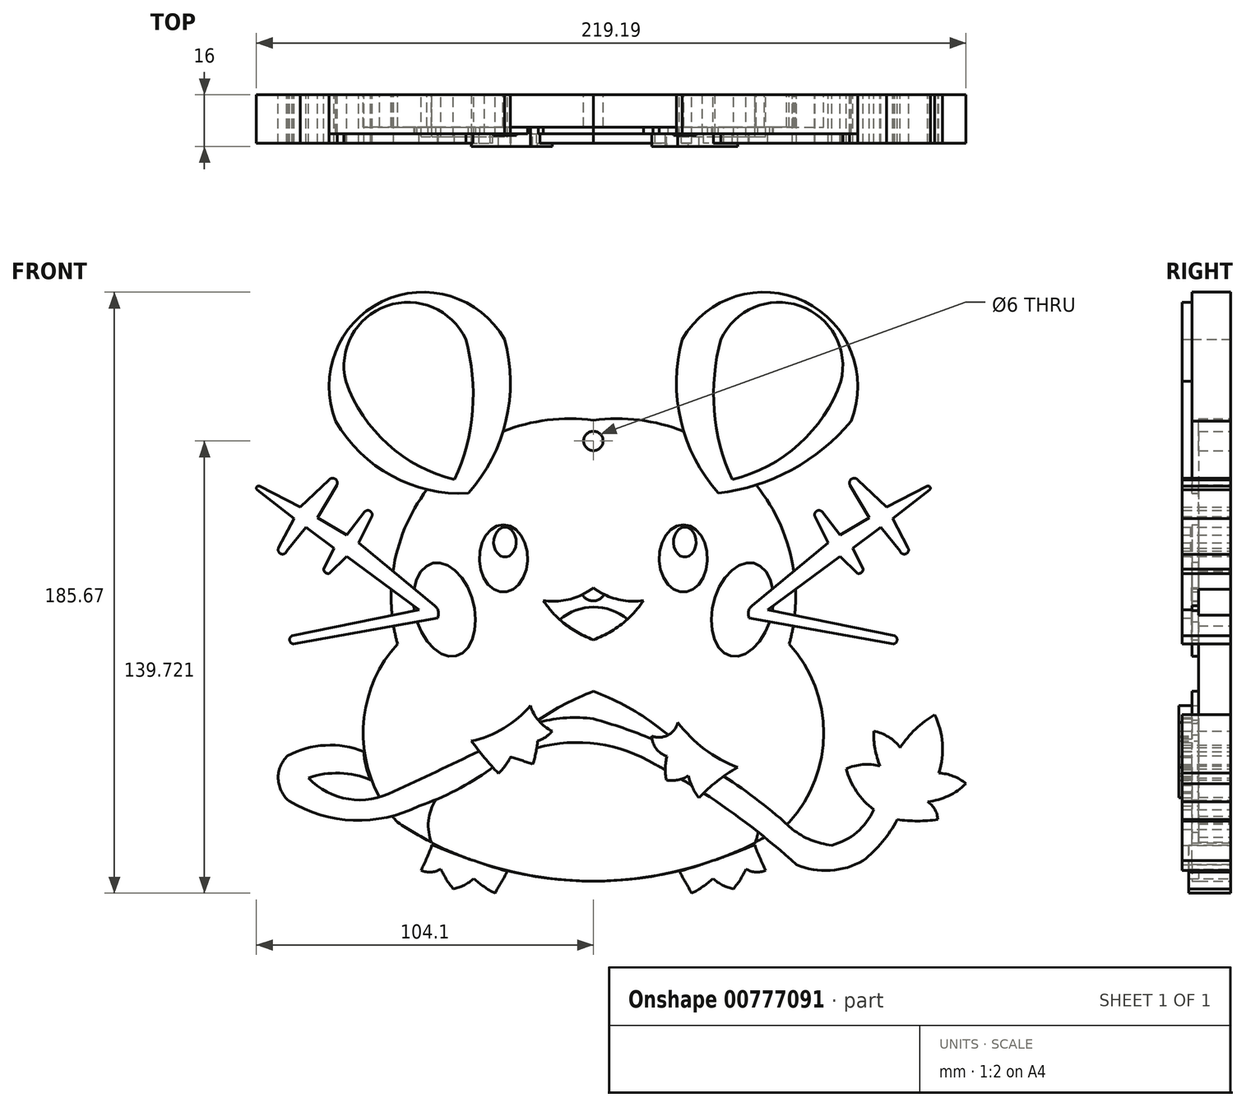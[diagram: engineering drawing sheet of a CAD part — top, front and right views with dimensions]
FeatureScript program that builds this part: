
annotation { "Feature Type Name" : "Feature", "Feature Type Description" : "" }
export const myFeature = defineFeature(function(context is Context, id is Id, definition is map)
    precondition{}
    {
        {
            var Q0;
            Q0=qCreatedBy(makeId("Front.planeOp"),FACE);
            var sketch = newSketch(context, id + "F0", { "sketchPlane" : qUnion([Q0])});
            skPoint(sketch, "E0", {"position": v(-60.51, 0) * mm});
            skPoint(sketch, "E1", {"position": v(0, 69.06) * mm});
            skArc(sketch, "E2", {"start": v(0, 69.06) * mm, "mid": v(-48.84, 50.82) * mm, "end": v(-60.51, 0) * mm});
            skLineSegment(sketch, "E3", {"start": v(0, 69.06) * mm, "end": v(0, -72.21) * mm, "construction": true});
            skArc(sketch, "E4.MirrorCS", {"start": v(0, 69.06) * mm, "mid": v(48.84, 50.82) * mm, "end": v(60.51, 0) * mm});
            skPoint(sketch, "E5", {"position": v(-60.51, -55.13) * mm});
            skArc(sketch, "E6", {"start": v(-60.51, 0) * mm, "mid": v(-71.12, -27.56) * mm, "end": v(-60.51, -55.13) * mm});
            skArc(sketch, "E7.MirrorCS", {"start": v(60.51, 0) * mm, "mid": v(71.12, -27.56) * mm, "end": v(60.51, -55.13) * mm});
            skArc(sketch, "E8", {"start": v(-60.51, -55.13) * mm, "mid": v(0, -73.32) * mm, "end": v(60.51, -55.13) * mm});
            skSolve(sketch);
        }
        {
            var Q0;
            Q0=qCreatedBy(makeId("Front.planeOp"),FACE);
            var sketch = newSketch(context, id + "F1", { "sketchPlane" : qUnion([Q0])});
            skEllipse(sketch, "E9", {"center": v(-27.78, 26.42) * mm, "majorRadius": 10.45 * mm, "minorRadius": 7.45 * mm, "majorAxis": v(0, 1)});
            skEllipse(sketch, "E10", {"center": v(-46, 10.64) * mm, "majorRadius": 14.77 * mm, "minorRadius": 9.16 * mm, "majorAxis": v(-0.25, 0.97)});
            skEllipse(sketch, "E11.MirrorC", {"center": v(46, 10.64) * mm, "majorRadius": 14.77 * mm, "minorRadius": 9.16 * mm, "majorAxis": v(0.25, 0.97)});
            skEllipse(sketch, "E12.MirrorC", {"center": v(27.78, 26.42) * mm, "majorRadius": 10.45 * mm, "minorRadius": 7.45 * mm, "majorAxis": v(0, 1)});
            skEllipse(sketch, "E13", {"center": v(-27.3, 31.45) * mm, "majorRadius": 4.6 * mm, "minorRadius": 3.5 * mm, "majorAxis": v(0, 1)});
            skPoint(sketch, "E14.endSnap0", {"position": v(-30.8, 31.45) * mm});
            skPoint(sketch, "E15", {"position": v(-34.3, 31.45) * mm});
            skPoint(sketch, "E16", {"position": v(21.25, 31.45) * mm});
            skPoint(sketch, "E17", {"position": v(28.25, 31.45) * mm});
            skPoint(sketch, "E18", {"position": v(-27.3, 36.05) * mm});
            skLineSegment(sketch, "E19", {"start": v(28.25, 36.05) * mm, "end": v(28.25, 40.65) * mm});
            skPoint(sketch, "E20", {"position": v(28.25, 36.05) * mm});
            skEllipse(sketch, "E21", {"center": v(28.25, 31.45) * mm, "majorRadius": 4.6 * mm, "minorRadius": 3.5 * mm, "majorAxis": v(0, 1)});
            skPoint(sketch, "E22", {"position": v(-23.8, 31.45) * mm});
            skPoint(sketch, "E23", {"position": v(24.75, 31.45) * mm});
            skPoint(sketch, "E24", {"position": v(31.75, 31.45) * mm});
            skPoint(sketch, "E14.end.orphan", {"position": v(-36.36, 31.45) * mm});
            skPoint(sketch, "E25", {"position": v(0, 17.34) * mm});
            skPoint(sketch, "E26", {"position": v(-18.45, 14.06) * mm});
            skArc(sketch, "E27", {"start": v(-18.45, 14.06) * mm, "mid": v(-8.83, 13.48) * mm, "end": v(0, 17.34) * mm});
            skArc(sketch, "E28.MirrorCS", {"start": v(18.45, 14.06) * mm, "mid": v(8.83, 13.48) * mm, "end": v(0, 17.34) * mm});
            skPoint(sketch, "E29", {"position": v(0, 0) * mm});
            skPoint(sketch, "E30", {"position": v(0, 1.29) * mm});
            skPoint(sketch, "E31", {"position": v(0, 10.13) * mm});
            skPoint(sketch, "E32", {"position": v(-5.69, 14.3) * mm});
            skArc(sketch, "E33", {"start": v(-5.69, 14.3) * mm, "mid": v(-3.15, 11.8) * mm, "end": v(0, 10.13) * mm});
            skArc(sketch, "E34.MirrorCS", {"start": v(5.69, 14.3) * mm, "mid": v(3.15, 11.8) * mm, "end": v(0, 10.13) * mm});
            skArc(sketch, "E35", {"start": v(-15.44, 13.38) * mm, "mid": v(-8.7, 6.08) * mm, "end": v(0, 1.29) * mm});
            skArc(sketch, "E36.MirrorCS", {"start": v(15.44, 13.38) * mm, "mid": v(8.7, 6.08) * mm, "end": v(0, 1.29) * mm});
            skPoint(sketch, "E37", {"position": v(-79.58, 68.87) * mm});
            skPoint(sketch, "E38", {"position": v(-38.6, 46.57) * mm});
            skPoint(sketch, "E39", {"position": v(-27.45, 94.11) * mm});
            skArc(sketch, "E40", {"start": v(-79.58, 68.87) * mm, "mid": v(-62.27, 51.88) * mm, "end": v(-38.6, 46.57) * mm});
            skArc(sketch, "E41", {"start": v(-38.6, 46.57) * mm, "mid": v(-27, 68.93) * mm, "end": v(-27.45, 94.11) * mm});
            skArc(sketch, "E42", {"start": v(-27.45, 94.11) * mm, "mid": v(-65.26, 105.75) * mm, "end": v(-79.58, 68.87) * mm});
            skArc(sketch, "E43.MirrorCS", {"start": v(38.6, 46.57) * mm, "mid": v(27, 68.93) * mm, "end": v(27.45, 94.11) * mm});
            skArc(sketch, "E44.MirrorCS", {"start": v(27.45, 94.11) * mm, "mid": v(65.26, 105.75) * mm, "end": v(79.58, 68.87) * mm});
            skArc(sketch, "E45", {"start": v(38.6, 46.57) * mm, "mid": v(61.26, 53.74) * mm, "end": v(79.58, 68.87) * mm});
            skPoint(sketch, "E46", {"position": v(0, -14.65) * mm});
            skPoint(sketch, "E47", {"position": v(-18.44, -24.49) * mm});
            skPoint(sketch, "E48", {"position": v(-49.92, -61.53) * mm});
            skPoint(sketch, "E49", {"position": v(-48.16, -47.4) * mm});
            skArc(sketch, "E50", {"start": v(0, -14.65) * mm, "mid": v(-9.54, -18.97) * mm, "end": v(-18.44, -24.49) * mm});
            skArc(sketch, "E51", {"start": v(-48.16, -47.4) * mm, "mid": v(-50.9, -54.23) * mm, "end": v(-49.92, -61.53) * mm});
            skLineSegment(sketch, "E52", {"start": v(-18.44, -24.49) * mm, "end": v(-48.16, -47.4) * mm});
            skArc(sketch, "E53.MirrorCS", {"start": v(0, -14.65) * mm, "mid": v(9.54, -18.97) * mm, "end": v(18.44, -24.49) * mm});
            skLineSegment(sketch, "E54.MirrorCS", {"start": v(18.44, -24.49) * mm, "end": v(48.16, -47.4) * mm});
            skArc(sketch, "E55.MirrorCS", {"start": v(48.16, -47.4) * mm, "mid": v(50.9, -54.23) * mm, "end": v(49.92, -61.53) * mm});
            skArc(sketch, "E56", {"start": v(-49.92, -61.53) * mm, "mid": v(0, -73.23) * mm, "end": v(49.92, -61.53) * mm});
            skSolve(sketch);
        }
        {
            var Q0;
            Q0=qCreatedBy(makeId("Front.planeOp"),FACE);
            var sketch = newSketch(context, id + "F2", { "sketchPlane" : qUnion([Q0])});
            skLineSegment(sketch, "E57", {"start": v(-48.16, 7.98) * mm, "end": v(-92.67, 0) * mm});
            skPoint(sketch, "E58", {"position": v(-93.06, 2.5) * mm});
            skPoint(sketch, "E59", {"position": v(-48.96, 11.76) * mm});
            skArc(sketch, "E60", {"start": v(-93.06, 2.5) * mm, "mid": v(-93.82, 1.1) * mm, "end": v(-92.67, 0) * mm});
            skArc(sketch, "E61", {"start": v(-48.16, 7.98) * mm, "mid": v(-47.9, 10.01) * mm, "end": v(-48.96, 11.76) * mm});
            skLineSegment(sketch, "E62", {"start": v(-93.06, 2.5) * mm, "end": v(-53.87, 10.6) * mm});
            skLineSegment(sketch, "E63", {"start": v(-53.87, 10.6) * mm, "end": v(-76.2, 27) * mm});
            skLineSegment(sketch, "E64", {"start": v(-76.2, 27) * mm, "end": v(-81.72, 21.76) * mm});
            skLineSegment(sketch, "E65", {"start": v(-48.96, 11.76) * mm, "end": v(-72.48, 31.21) * mm});
            skLineSegment(sketch, "E66", {"start": v(-72.48, 31.21) * mm, "end": v(-68.43, 39.4) * mm});
            skPoint(sketch, "E67", {"position": v(-83.3, 23.07) * mm});
            skPoint(sketch, "E68", {"position": v(-70.75, 40.72) * mm});
            skPoint(sketch, "E69", {"position": v(-79.3, 48.99) * mm});
            skPoint(sketch, "E70", {"position": v(-81.72, 50.64) * mm});
            skPoint(sketch, "E71", {"position": v(-103.83, 47.6) * mm});
            skPoint(sketch, "E72", {"position": v(-103.15, 48.71) * mm});
            skPoint(sketch, "E73", {"position": v(-97.22, 29.69) * mm});
            skPoint(sketch, "E74", {"position": v(-94.74, 28.72) * mm});
            skLineSegment(sketch, "E75", {"start": v(-80.13, 29.55) * mm, "end": v(-87.57, 35.2) * mm});
            skLineSegment(sketch, "E76", {"start": v(-79.3, 48.99) * mm, "end": v(-85.23, 38.92) * mm});
            skLineSegment(sketch, "E77", {"start": v(-85.23, 38.92) * mm, "end": v(-76.2, 33.6) * mm});
            skLineSegment(sketch, "E78", {"start": v(-76.2, 33.6) * mm, "end": v(-70.75, 40.72) * mm});
            skLineSegment(sketch, "E79", {"start": v(-97.22, 29.69) * mm, "end": v(-92.4, 38.79) * mm});
            skLineSegment(sketch, "E80", {"start": v(-92.4, 38.79) * mm, "end": v(-103.83, 47.6) * mm});
            skLineSegment(sketch, "E81", {"start": v(-103.15, 48.71) * mm, "end": v(-90.6, 42.23) * mm});
            skLineSegment(sketch, "E82", {"start": v(-90.6, 42.23) * mm, "end": v(-81.72, 50.64) * mm});
            skArc(sketch, "E83", {"start": v(-103.15, 48.71) * mm, "mid": v(-104, 48.48) * mm, "end": v(-103.83, 47.6) * mm});
            skArc(sketch, "E84", {"start": v(-97.22, 29.69) * mm, "mid": v(-96.52, 27.81) * mm, "end": v(-94.74, 28.72) * mm});
            skLineSegment(sketch, "E85", {"start": v(-94.74, 28.72) * mm, "end": v(-88.74, 36.09) * mm});
            skLineSegment(sketch, "E86", {"start": v(-88.74, 36.09) * mm, "end": v(-87.57, 35.2) * mm});
            skArc(sketch, "E87", {"start": v(-79.3, 48.99) * mm, "mid": v(-79.73, 50.94) * mm, "end": v(-81.72, 50.64) * mm});
            skArc(sketch, "E88", {"start": v(-68.43, 39.4) * mm, "mid": v(-69.02, 41.07) * mm, "end": v(-70.75, 40.72) * mm});
            skArc(sketch, "E89", {"start": v(-83.3, 23.07) * mm, "mid": v(-82.8, 22.05) * mm, "end": v(-81.72, 21.76) * mm});
            skLineSegment(sketch, "E90", {"start": v(-80.13, 29.55) * mm, "end": v(-83.3, 23.07) * mm});
            skLineSegment(sketch, "E91.MirrorCS", {"start": v(103.15, 48.71) * mm, "end": v(90.6, 42.23) * mm});
            skArc(sketch, "E92.MirrorCS", {"start": v(103.15, 48.71) * mm, "mid": v(104, 48.48) * mm, "end": v(103.83, 47.6) * mm});
            skLineSegment(sketch, "E93.MirrorCS", {"start": v(92.4, 38.79) * mm, "end": v(103.83, 47.6) * mm});
            skLineSegment(sketch, "E94.MirrorCS", {"start": v(90.6, 42.23) * mm, "end": v(81.72, 50.64) * mm});
            skArc(sketch, "E95.MirrorCS", {"start": v(79.3, 48.99) * mm, "mid": v(79.73, 50.94) * mm, "end": v(81.72, 50.64) * mm});
            skLineSegment(sketch, "E96.MirrorCS", {"start": v(79.3, 48.99) * mm, "end": v(85.23, 38.92) * mm});
            skLineSegment(sketch, "E97.MirrorCS", {"start": v(97.22, 29.69) * mm, "end": v(92.4, 38.79) * mm});
            skArc(sketch, "E98.MirrorCS", {"start": v(97.22, 29.69) * mm, "mid": v(96.52, 27.81) * mm, "end": v(94.74, 28.72) * mm});
            skLineSegment(sketch, "E99.MirrorCS", {"start": v(94.74, 28.72) * mm, "end": v(88.74, 36.09) * mm});
            skLineSegment(sketch, "E100.MirrorCS", {"start": v(80.13, 29.55) * mm, "end": v(87.57, 35.2) * mm});
            skLineSegment(sketch, "E101.MirrorCS", {"start": v(88.74, 36.09) * mm, "end": v(87.57, 35.2) * mm});
            skLineSegment(sketch, "E102.MirrorCS", {"start": v(80.13, 29.55) * mm, "end": v(83.3, 23.07) * mm});
            skArc(sketch, "E103.MirrorCS", {"start": v(83.3, 23.07) * mm, "mid": v(82.8, 22.05) * mm, "end": v(81.72, 21.76) * mm});
            skLineSegment(sketch, "E104.MirrorCS", {"start": v(76.2, 27) * mm, "end": v(81.72, 21.76) * mm});
            skLineSegment(sketch, "E105.MirrorCS", {"start": v(53.87, 10.6) * mm, "end": v(76.2, 27) * mm});
            skLineSegment(sketch, "E106.MirrorCS", {"start": v(76.2, 33.6) * mm, "end": v(70.75, 40.72) * mm});
            skArc(sketch, "E107.MirrorCS", {"start": v(68.43, 39.4) * mm, "mid": v(69.02, 41.07) * mm, "end": v(70.75, 40.72) * mm});
            skLineSegment(sketch, "E108.MirrorCS", {"start": v(72.48, 31.21) * mm, "end": v(68.43, 39.4) * mm});
            skLineSegment(sketch, "E109.MirrorCS", {"start": v(48.96, 11.76) * mm, "end": v(72.48, 31.21) * mm});
            skArc(sketch, "E110.MirrorCS", {"start": v(48.16, 7.98) * mm, "mid": v(47.9, 10.01) * mm, "end": v(48.96, 11.76) * mm});
            skLineSegment(sketch, "E111.MirrorCS", {"start": v(48.16, 7.98) * mm, "end": v(92.67, 0) * mm});
            skLineSegment(sketch, "E112.MirrorCS", {"start": v(93.06, 2.5) * mm, "end": v(53.87, 10.6) * mm});
            skArc(sketch, "E113.MirrorCS", {"start": v(93.06, 2.5) * mm, "mid": v(93.82, 1.1) * mm, "end": v(92.67, 0) * mm});
            skPoint(sketch, "E114", {"position": v(-70.89, -33.3) * mm});
            skPoint(sketch, "E115", {"position": v(-94.5, -34.6) * mm});
            skPoint(sketch, "E116", {"position": v(-94, -48.54) * mm});
            skPoint(sketch, "E117", {"position": v(-53.84, -50.01) * mm});
            skPoint(sketch, "E118", {"position": v(-31.87, -38.7) * mm});
            skPoint(sketch, "E119", {"position": v(19.1, -37.23) * mm});
            skPoint(sketch, "E120", {"position": v(62.71, -68.21) * mm});
            skPoint(sketch, "E121", {"position": v(83.37, -66.9) * mm});
            skPoint(sketch, "E122", {"position": v(93.86, -54.29) * mm});
            skPoint(sketch, "E123", {"position": v(106.4, -54.29) * mm});
            skPoint(sketch, "E124", {"position": v(103.29, -48.74) * mm});
            skPoint(sketch, "E125", {"position": v(115.1, -43.17) * mm});
            skPoint(sketch, "E126", {"position": v(106.73, -39.89) * mm});
            skPoint(sketch, "E127", {"position": v(105.42, -21.85) * mm});
            skPoint(sketch, "E128", {"position": v(94.76, -32.02) * mm});
            skPoint(sketch, "E129", {"position": v(86.57, -26.94) * mm});
            skPoint(sketch, "E130", {"position": v(88.54, -37.76) * mm});
            skPoint(sketch, "E131", {"position": v(78.04, -38.58) * mm});
            skPoint(sketch, "E132", {"position": v(86.57, -51.2) * mm});
            skPoint(sketch, "E133", {"position": v(73.62, -62.18) * mm});
            skPoint(sketch, "E134", {"position": v(61.49, -57.26) * mm});
            skPoint(sketch, "E135", {"position": v(0, -23.17) * mm});
            skPoint(sketch, "E136", {"position": v(-18.84, -24.8) * mm});
            skArc(sketch, "E137", {"start": v(94.76, -32.02) * mm, "mid": v(91.14, -28.71) * mm, "end": v(86.57, -26.94) * mm});
            skArc(sketch, "E138", {"start": v(105.42, -21.85) * mm, "mid": v(99.52, -26.34) * mm, "end": v(94.76, -32.02) * mm});
            skArc(sketch, "E139", {"start": v(106.73, -39.89) * mm, "mid": v(107.82, -30.74) * mm, "end": v(105.42, -21.85) * mm});
            skArc(sketch, "E140", {"start": v(115.1, -43.17) * mm, "mid": v(111.17, -40.86) * mm, "end": v(106.73, -39.89) * mm});
            skArc(sketch, "E141", {"start": v(103.29, -48.74) * mm, "mid": v(109.66, -46.95) * mm, "end": v(115.1, -43.17) * mm});
            skArc(sketch, "E142", {"start": v(106.4, -54.29) * mm, "mid": v(105.49, -51.15) * mm, "end": v(103.29, -48.74) * mm});
            skArc(sketch, "E143", {"start": v(93.86, -54.29) * mm, "mid": v(100.13, -54.7) * mm, "end": v(106.4, -54.29) * mm});
            skArc(sketch, "E144", {"start": v(78.04, -38.58) * mm, "mid": v(81.27, -45.59) * mm, "end": v(86.57, -51.2) * mm});
            skArc(sketch, "E145", {"start": v(88.54, -37.76) * mm, "mid": v(83.22, -37.27) * mm, "end": v(78.04, -38.58) * mm});
            skArc(sketch, "E146", {"start": v(86.57, -26.94) * mm, "mid": v(87.01, -32.44) * mm, "end": v(88.54, -37.76) * mm});
            skArc(sketch, "E147", {"start": v(73.62, -62.18) * mm, "mid": v(81.39, -58.21) * mm, "end": v(86.57, -51.2) * mm});
            skArc(sketch, "E148", {"start": v(61.49, -57.26) * mm, "mid": v(67.2, -60.57) * mm, "end": v(73.62, -62.18) * mm});
            skArc(sketch, "E149", {"start": v(61.49, -57.26) * mm, "mid": v(32.8, -36.5) * mm, "end": v(0, -23.17) * mm});
            skArc(sketch, "E150", {"start": v(0, -23.17) * mm, "mid": v(-9.51, -22.93) * mm, "end": v(-18.84, -24.8) * mm});
            skArc(sketch, "E151", {"start": v(83.37, -66.9) * mm, "mid": v(89.26, -61.14) * mm, "end": v(93.86, -54.29) * mm});
            skArc(sketch, "E152", {"start": v(62.71, -68.21) * mm, "mid": v(73.2, -69.99) * mm, "end": v(83.37, -66.9) * mm});
            skArc(sketch, "E153", {"start": v(62.71, -68.21) * mm, "mid": v(41.87, -51.37) * mm, "end": v(19.1, -37.23) * mm});
            skArc(sketch, "E154", {"start": v(19.1, -37.23) * mm, "mid": v(-6.6, -30.48) * mm, "end": v(-31.87, -38.7) * mm});
            skArc(sketch, "E155", {"start": v(-53.84, -50.01) * mm, "mid": v(-42.41, -45.22) * mm, "end": v(-31.87, -38.7) * mm});
            skArc(sketch, "E156", {"start": v(-94, -48.54) * mm, "mid": v(-74.11, -54.48) * mm, "end": v(-53.84, -50.01) * mm});
            skArc(sketch, "E157", {"start": v(-94.5, -34.6) * mm, "mid": v(-97.37, -41.68) * mm, "end": v(-94, -48.54) * mm});
            skArc(sketch, "E158", {"start": v(-70.89, -33.3) * mm, "mid": v(-82.84, -31.32) * mm, "end": v(-94.5, -34.6) * mm});
            skArc(sketch, "E159", {"start": v(-70.89, -33.3) * mm, "mid": v(-70.25, -37.76) * mm, "end": v(-68.8, -42.03) * mm});
            skArc(sketch, "E160", {"start": v(-68.8, -42.03) * mm, "mid": v(-78.34, -39.94) * mm, "end": v(-88.02, -41.35) * mm});
            skArc(sketch, "E161", {"start": v(-88.02, -41.35) * mm, "mid": v(-75.61, -47.94) * mm, "end": v(-61.77, -45.54) * mm});
            skArc(sketch, "E162", {"start": v(-61.77, -45.54) * mm, "mid": v(-40.15, -35.48) * mm, "end": v(-18.84, -24.8) * mm});
            skPoint(sketch, "E163", {"position": v(-49.8, -62.04) * mm});
            skPoint(sketch, "E164", {"position": v(-52.75, -69.75) * mm});
            skPoint(sketch, "E165", {"position": v(-47.17, -69.9) * mm});
            skPoint(sketch, "E166", {"position": v(-43.4, -75.48) * mm});
            skPoint(sketch, "E167", {"position": v(-36.52, -72.53) * mm});
            skPoint(sketch, "E168", {"position": v(-30.45, -77.29) * mm});
            skPoint(sketch, "E169", {"position": v(-26.85, -70.24) * mm});
            skArc(sketch, "E170", {"start": v(-49.8, -62.04) * mm, "mid": v(-51.37, -65.86) * mm, "end": v(-52.75, -69.75) * mm});
            skArc(sketch, "E171", {"start": v(-52.75, -69.75) * mm, "mid": v(-49.97, -70.3) * mm, "end": v(-47.17, -69.9) * mm});
            skArc(sketch, "E172", {"start": v(-47.17, -69.9) * mm, "mid": v(-45.46, -72.81) * mm, "end": v(-43.4, -75.48) * mm});
            skArc(sketch, "E173", {"start": v(-43.4, -75.48) * mm, "mid": v(-39.78, -74.42) * mm, "end": v(-36.52, -72.53) * mm});
            skArc(sketch, "E174", {"start": v(-36.52, -72.53) * mm, "mid": v(-33.57, -75.02) * mm, "end": v(-30.45, -77.29) * mm});
            skArc(sketch, "E175", {"start": v(-30.45, -77.29) * mm, "mid": v(-28.52, -73.83) * mm, "end": v(-26.85, -70.24) * mm});
            skArc(sketch, "E176.MirrorCS", {"start": v(49.8, -62.04) * mm, "mid": v(51.37, -65.86) * mm, "end": v(52.75, -69.75) * mm});
            skArc(sketch, "E177.MirrorCS", {"start": v(52.75, -69.75) * mm, "mid": v(49.97, -70.3) * mm, "end": v(47.17, -69.9) * mm});
            skArc(sketch, "E178.MirrorCS", {"start": v(47.17, -69.9) * mm, "mid": v(45.46, -72.81) * mm, "end": v(43.4, -75.48) * mm});
            skArc(sketch, "E179.MirrorCS", {"start": v(43.4, -75.48) * mm, "mid": v(39.78, -74.42) * mm, "end": v(36.52, -72.53) * mm});
            skArc(sketch, "E180.MirrorCS", {"start": v(36.52, -72.53) * mm, "mid": v(33.57, -75.02) * mm, "end": v(30.45, -77.29) * mm});
            skArc(sketch, "E181.MirrorCS", {"start": v(30.45, -77.29) * mm, "mid": v(28.52, -73.83) * mm, "end": v(26.85, -70.24) * mm});
            skPoint(sketch, "E182", {"position": v(-42.87, 50.73) * mm});
            skPoint(sketch, "E183", {"position": v(-39.4, 94.09) * mm});
            skPoint(sketch, "E184", {"position": v(-76.49, 81.1) * mm});
            skArc(sketch, "E185", {"start": v(-42.87, 50.73) * mm, "mid": v(-37.35, 72.1) * mm, "end": v(-39.4, 94.09) * mm});
            skArc(sketch, "E186", {"start": v(-76.49, 81.1) * mm, "mid": v(-63.51, 61.68) * mm, "end": v(-42.87, 50.73) * mm});
            skArc(sketch, "E187", {"start": v(-39.4, 94.09) * mm, "mid": v(-63.83, 104.42) * mm, "end": v(-76.49, 81.1) * mm});
            skArc(sketch, "E188.MirrorCS", {"start": v(76.49, 81.1) * mm, "mid": v(63.51, 61.68) * mm, "end": v(42.87, 50.73) * mm});
            skArc(sketch, "E189.MirrorCS", {"start": v(39.4, 94.09) * mm, "mid": v(63.83, 104.42) * mm, "end": v(76.49, 81.1) * mm});
            skArc(sketch, "E190.MirrorCS", {"start": v(42.87, 50.73) * mm, "mid": v(37.35, 72.1) * mm, "end": v(39.4, 94.09) * mm});
            skArc(sketch, "E191", {"start": v(-49.73, -62) * mm, "mid": v(-38.7, -67.26) * mm, "end": v(-26.85, -70.24) * mm});
            skArc(sketch, "E192.MirrorCS", {"start": v(49.73, -62) * mm, "mid": v(38.7, -67.26) * mm, "end": v(26.85, -70.24) * mm});
            skLineSegment(sketch, "E193", {"start": v(76.2, 33.6) * mm, "end": v(85.23, 38.92) * mm});
            skSolve(sketch);
        }
        {
            var Q0;
            Q0=qCreatedBy(makeId("Front.planeOp"),FACE);
            var sketch = newSketch(context, id + "F3", { "sketchPlane" : qUnion([Q0])});
            skCircle(sketch, "E194", {"center": v(0, 62.7) * mm, "radius": 4 * mm});
            skSolve(sketch);
        }
        {
            var Q0;
            Q0=qSketchRegion(id+"F0",true);
            extrude(context, id + "F4", {"entities" : qUnion([Q0]), "depth" : 10 * mm, "offsetDistance" : 25 * mm});
        }
        {
            var Q0;
            Q0=qSketchRegion(id+"F1",true);
            extrude(context, id + "F5", {"entities" : qUnion([Q0]), "operationType" : NewBodyOperationType.ADD, "depth" : 12 * mm, "offsetDistance" : 25 * mm});
        }
        {
            var Q0;
            Q0=makeQuery(id+"F5.opExtrude","CAP_FACE",FACE,{"disambiguationData":[OSD([sQuery(id+"F1.wireOp",EDGE,"E27"),sQuery(id+"F1.wireOp",EDGE,"E28.MirrorCS"),sQuery(id+"F1.wireOp",EDGE,"E35"),sQuery(id+"F1.wireOp",EDGE,"E36.MirrorCS")])],"isStart":false});
            var sketch = newSketch(context, id + "F6", { "sketchPlane" : qUnion([Q0])});
            skArc(sketch, "E195", {"start": v(10.55, 7.64) * mm, "mid": v(0.05, 11.38) * mm, "end": v(-10.39, 7.49) * mm});
            skArc(sketch, "E196", {"start": v(-10.39, 7.49) * mm, "mid": v(-5.46, 3.94) * mm, "end": v(0, 1.29) * mm});
            skArc(sketch, "E197", {"start": v(0, 1.29) * mm, "mid": v(5.59, 3.94) * mm, "end": v(10.55, 7.64) * mm});
            skSolve(sketch);
        }
        {
            var Q0;
            Q0=makeQuery(id+"F6.imprint","IMPRINT",FACE,{"disambiguationData":[TD([[makeQuery(id+"F6.imprint","IMPRINT",EDGE,{"derivedFrom":sQuery(id+"F6.wireOp",EDGE,"E195")}),1.0]])]});
            extrude(context, id + "F7", {"entities" : qUnion([Q0]), "operationType" : NewBodyOperationType.ADD, "depth" : 0.1 * mm, "offsetDistance" : 25 * mm});
        }
        {
            var Q0;
            Q0=makeQuery(id+"F5.boolean.opBoolean","SPLIT",FACE,{"disambiguationData":[TD([makeQuery(id+"F5.opExtrude","SWEPT_FACE",FACE,{"disambiguationData":[OSD([sQuery(id+"F1.wireOp",EDGE,"E13")])]})])],"derivedFrom":makeQuery(id+"F4.opExtrude","CAP_FACE",FACE,{"disambiguationData":[OSD([sQuery(id+"F0.wireOp",EDGE,"E2"),sQuery(id+"F0.wireOp",EDGE,"E4.MirrorCS"),sQuery(id+"F0.wireOp",EDGE,"E6"),sQuery(id+"F0.wireOp",EDGE,"E7.MirrorCS"),sQuery(id+"F0.wireOp",EDGE,"E8")])],"isStart":false})});
            var Q1;
            Q1=makeQuery(id+"F5.boolean.opBoolean","SPLIT",FACE,{"disambiguationData":[TD([makeQuery(id+"F5.opExtrude","SWEPT_FACE",FACE,{"disambiguationData":[OSD([sQuery(id+"F1.wireOp",EDGE,"E21")])]})])],"derivedFrom":makeQuery(id+"F4.opExtrude","CAP_FACE",FACE,{"disambiguationData":[OSD([sQuery(id+"F0.wireOp",EDGE,"E2"),sQuery(id+"F0.wireOp",EDGE,"E4.MirrorCS"),sQuery(id+"F0.wireOp",EDGE,"E6"),sQuery(id+"F0.wireOp",EDGE,"E7.MirrorCS"),sQuery(id+"F0.wireOp",EDGE,"E8")])],"isStart":false})});
            extrude(context, id + "F8", {"entities" : qUnion([Q0, Q1]), "operationType" : NewBodyOperationType.ADD, "depth" : 2.5 * mm, "offsetDistance" : 25 * mm});
        }
        {
            var Q0;
            {var subQ0=sQuery(id+"F1.wireOp",EDGE,"E35");var subQ1=sQuery(id+"F1.wireOp",EDGE,"E28.MirrorCS");var subQ2=sQuery(id+"F1.wireOp",EDGE,"E36.MirrorCS");var subQ3=sQuery(id+"F1.wireOp",EDGE,"E27");var subQ4=makeQuery(id+"F5.opExtrude","CAP_FACE",FACE,{"disambiguationData":[OSD([subQ3,subQ1,subQ0,subQ2])],"isStart":false});Q0=makeQuery(id+"F7.boolean.opBoolean","SPLIT",FACE,{"disambiguationData":[TD([makeQuery(id+"F5.opExtrude","SWEPT_FACE",FACE,{"disambiguationData":[OSD([subQ3])]}),subQ4,makeQuery(id+"F5.opExtrude","SWEPT_FACE",FACE,{"disambiguationData":[OSD([subQ1])]}),makeQuery(id+"F5.opExtrude","SWEPT_FACE",FACE,{"disambiguationData":[OSD([subQ0])]}),makeQuery(id+"F5.opExtrude","SWEPT_FACE",FACE,{"disambiguationData":[OSD([subQ2])]}),makeQuery(id+"F7.opExtrude","SWEPT_FACE",FACE,{"disambiguationData":[OSD([sQuery(id+"F6.wireOp",EDGE,"E195")])]}),makeQuery(id+"F7.opExtrude","SWEPT_FACE",FACE,{"disambiguationData":[OSD([sQuery(id+"F6.wireOp",EDGE,"E196")])]}),makeQuery(id+"F7.opExtrude","SWEPT_FACE",FACE,{"disambiguationData":[OSD([sQuery(id+"F6.wireOp",EDGE,"E197")])]})])],"derivedFrom":subQ4});}
            var sketch = newSketch(context, id + "F9", { "sketchPlane" : qUnion([Q0])});
            skArc(sketch, "E198", {"start": v(-3.43, 15.23) * mm, "mid": v(-0.05, 13.27) * mm, "end": v(3.3, 15.3) * mm});
            skSolve(sketch);
        }
        {
            var Q0;
            {var subQ0=sQuery(id+"F9.wireOp",EDGE,"E198");Q0=makeQuery(id+"F9.imprint","IMPRINT",FACE,{"disambiguationData":[TD([[makeQuery(id+"F9.imprint","IMPRINT",EDGE,{"derivedFrom":subQ0}),1.0]])]});}
            extrude(context, id + "F10", {"entities" : qUnion([Q0]), "operationType" : NewBodyOperationType.ADD, "depth" : 0.1 * mm, "offsetDistance" : 25 * mm});
        }
        {
            var Q0;
            Q0=qSketchRegion(id+"F2",true);
            extrude(context, id + "F11", {"entities" : qUnion([Q0]), "operationType" : NewBodyOperationType.ADD, "depth" : 15 * mm, "offsetDistance" : 25 * mm});
        }
        {
            var Q0;
            Q0=qCreatedBy(makeId("Front.planeOp"),FACE);
            var sketch = newSketch(context, id + "F12", { "sketchPlane" : qUnion([Q0])});
            skPoint(sketch, "E199", {"position": v(-37.67, -29.99) * mm});
            skPoint(sketch, "E200", {"position": v(-29.34, -40.02) * mm});
            skPoint(sketch, "E201", {"position": v(-25.55, -34.9) * mm});
            skPoint(sketch, "E202", {"position": v(-18.73, -37.18) * mm});
            skPoint(sketch, "E203", {"position": v(-17.22, -29.99) * mm});
            skPoint(sketch, "E204", {"position": v(-12.68, -26.96) * mm});
            skPoint(sketch, "E205", {"position": v(-19.5, -19) * mm});
            skArc(sketch, "E206", {"start": v(-37.67, -29.99) * mm, "mid": v(-33.66, -35.13) * mm, "end": v(-29.34, -40.02) * mm});
            skArc(sketch, "E207", {"start": v(-29.34, -40.02) * mm, "mid": v(-27.24, -37.61) * mm, "end": v(-25.55, -34.9) * mm});
            skArc(sketch, "E208", {"start": v(-18.73, -37.18) * mm, "mid": v(-22.12, -35.99) * mm, "end": v(-25.55, -34.9) * mm});
            skArc(sketch, "E209", {"start": v(-18.73, -37.18) * mm, "mid": v(-17.77, -33.63) * mm, "end": v(-17.22, -29.99) * mm});
            skArc(sketch, "E210", {"start": v(-17.22, -29.99) * mm, "mid": v(-14.74, -28.78) * mm, "end": v(-12.68, -26.96) * mm});
            skArc(sketch, "E211", {"start": v(-19.5, -19) * mm, "mid": v(-16.91, -23.7) * mm, "end": v(-12.68, -26.96) * mm});
            skArc(sketch, "E212", {"start": v(-37.67, -29.99) * mm, "mid": v(-27.64, -26.05) * mm, "end": v(-19.5, -19) * mm});
            skPoint(sketch, "E213", {"position": v(18.06, -28.5) * mm});
            skPoint(sketch, "E214", {"position": v(26.1, -24.22) * mm});
            skPoint(sketch, "E215", {"position": v(22.77, -34.69) * mm});
            skPoint(sketch, "E216", {"position": v(22.58, -42.07) * mm});
            skPoint(sketch, "E217", {"position": v(29.4, -40.75) * mm});
            skPoint(sketch, "E218", {"position": v(32.61, -47.56) * mm});
            skPoint(sketch, "E219", {"position": v(44.54, -38.1) * mm});
            skArc(sketch, "E220", {"start": v(18.06, -28.5) * mm, "mid": v(23.04, -28.16) * mm, "end": v(26.1, -24.22) * mm});
            skArc(sketch, "E221", {"start": v(18.06, -28.5) * mm, "mid": v(19.4, -32.37) * mm, "end": v(22.77, -34.69) * mm});
            skArc(sketch, "E222", {"start": v(22.77, -34.69) * mm, "mid": v(22.2, -38.37) * mm, "end": v(22.58, -42.07) * mm});
            skArc(sketch, "E223", {"start": v(22.58, -42.07) * mm, "mid": v(26.1, -42.02) * mm, "end": v(29.4, -40.75) * mm});
            skArc(sketch, "E224", {"start": v(29.4, -40.75) * mm, "mid": v(30.62, -44.33) * mm, "end": v(32.61, -47.56) * mm});
            skArc(sketch, "E225", {"start": v(44.54, -38.1) * mm, "mid": v(38.24, -42.4) * mm, "end": v(32.61, -47.56) * mm});
            skArc(sketch, "E226", {"start": v(26.1, -24.22) * mm, "mid": v(34.32, -32.49) * mm, "end": v(44.54, -38.1) * mm});
            skSolve(sketch);
        }
        {
            var Q0;
            Q0=qSketchRegion(id+"F12",true);
            extrude(context, id + "F13", {"entities" : qUnion([Q0]), "operationType" : NewBodyOperationType.ADD, "depth" : 16 * mm, "offsetDistance" : 25 * mm});
        }
        {
            var Q0;
            Q0=qCreatedBy(makeId("Front.planeOp"),FACE);
            var sketch = newSketch(context, id + "F14", { "sketchPlane" : qUnion([Q0])});
            skPoint(sketch, "E227", {"position": v(-49.85, -62.09) * mm});
            skPoint(sketch, "E228", {"position": v(-53.24, -70) * mm});
            skPoint(sketch, "E229", {"position": v(-26.56, -70.23) * mm});
            skPoint(sketch, "E230", {"position": v(-30.4, -77.02) * mm});
            skPoint(sketch, "E231", {"position": v(-36.96, -72.5) * mm});
            skPoint(sketch, "E232", {"position": v(-43.3, -75.66) * mm});
            skPoint(sketch, "E233", {"position": v(-47.14, -69.55) * mm});
            skArc(sketch, "E234", {"start": v(-53.24, -70) * mm, "mid": v(-51.43, -66.1) * mm, "end": v(-49.85, -62.09) * mm});
            skArc(sketch, "E235", {"start": v(-53.24, -70) * mm, "mid": v(-50.14, -70.5) * mm, "end": v(-47.14, -69.55) * mm});
            skArc(sketch, "E236", {"start": v(-47.14, -69.55) * mm, "mid": v(-45.4, -72.73) * mm, "end": v(-43.3, -75.66) * mm});
            skArc(sketch, "E237", {"start": v(-43.3, -75.66) * mm, "mid": v(-39.9, -74.52) * mm, "end": v(-36.96, -72.5) * mm});
            skArc(sketch, "E238", {"start": v(-36.96, -72.5) * mm, "mid": v(-33.82, -74.96) * mm, "end": v(-30.4, -77.02) * mm});
            skArc(sketch, "E239", {"start": v(-30.4, -77.02) * mm, "mid": v(-28.44, -73.64) * mm, "end": v(-26.56, -70.23) * mm});
            skArc(sketch, "E240", {"start": v(-49.85, -62.09) * mm, "mid": v(-38.32, -66.5) * mm, "end": v(-26.56, -70.23) * mm});
            skLineSegment(sketch, "E241", {"start": v(0, -50.56) * mm, "end": v(0, -83.35) * mm, "construction": true});
            skArc(sketch, "E242.MirrorCS", {"start": v(30.4, -77.02) * mm, "mid": v(28.44, -73.64) * mm, "end": v(26.56, -70.23) * mm});
            skArc(sketch, "E243.MirrorCS", {"start": v(36.96, -72.5) * mm, "mid": v(33.82, -74.96) * mm, "end": v(30.4, -77.02) * mm});
            skArc(sketch, "E244.MirrorCS", {"start": v(43.3, -75.66) * mm, "mid": v(39.9, -74.52) * mm, "end": v(36.96, -72.5) * mm});
            skArc(sketch, "E245.MirrorCS", {"start": v(47.14, -69.55) * mm, "mid": v(45.4, -72.73) * mm, "end": v(43.3, -75.66) * mm});
            skArc(sketch, "E246.MirrorCS", {"start": v(53.24, -70) * mm, "mid": v(50.14, -70.5) * mm, "end": v(47.14, -69.55) * mm});
            skArc(sketch, "E247.MirrorCS", {"start": v(53.24, -70) * mm, "mid": v(51.43, -66.1) * mm, "end": v(49.85, -62.09) * mm});
            skArc(sketch, "E248.MirrorCS", {"start": v(49.85, -62.09) * mm, "mid": v(38.32, -66.5) * mm, "end": v(26.56, -70.23) * mm});
            skSolve(sketch);
        }
        {
            var Q0;
            Q0=qSketchRegion(id+"F14",true);
            extrude(context, id + "F15", {"entities" : qUnion([Q0]), "operationType" : NewBodyOperationType.ADD, "depth" : 13 * mm, "offsetDistance" : 25 * mm});
        }
        {
            var Q0;
            Q0=sQuery(id+"F3.wireOp",VERTEX,"E194.center");
            var Q1;
            Q1=makeQuery(id+"F4.opExtrude","SWEPT_BODY",BODY,{"disambiguationData":[OSD([sQuery(id+"F0.wireOp",EDGE,"E2"),sQuery(id+"F0.wireOp",EDGE,"E4.MirrorCS"),sQuery(id+"F0.wireOp",EDGE,"E6"),sQuery(id+"F0.wireOp",EDGE,"E7.MirrorCS"),sQuery(id+"F0.wireOp",EDGE,"E8")])]});
            hole(context, id + "F16", {"style" : HoleStyle.C_BORE, "endStyle" : HoleEndStyle.THROUGH, "oppositeDirection" : true, "holeDiameter" : 6 * mm, "cBoreDiameter" : 6 * mm, "cBoreDepth" : 5 * mm, "isTappedThrough" : true, "tappedDepth" : 12 * mm, "tapClearance" : 3, "startFromSketch" : true, "locations" : qUnion([Q0]), "scope" : qUnion([Q1])});
        }
    });
